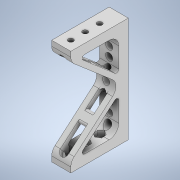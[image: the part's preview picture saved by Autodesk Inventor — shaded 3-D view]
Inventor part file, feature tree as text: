
AUTODESK INVENTOR PART (.ipt)
format: ipt  version: 2020 (Build 240168000, 168)  size: 472,576 bytes
history: native  units: in
note: dims shown in document units (in); Inventor stores cm internally (conversion verified against a paired STEP export)
features: extrude x10, sketch x10, plane x4, fillet x2, mirror x1
ambient origin geometry x8: Origin, YZ Plane, XZ Plane, XY Plane, X Axis, Y Axis, Z Axis, Center Point
bodies: Solid1 (feature_tree)
feature tree (27):
  extrude  "Extrusion1"  Depth=5.5in
  extrude  "Extrusion2"  Depth=0.5in
  fillet  "Fillet1"  Radius=0.5in
  extrude  "Extrusion3"  Depth=0.25in
  fillet  "Fillet2"  Radius=0.25in
  extrude  "Extrusion4"  Depth=0.5in
  plane  "Work Plane1"
  extrude  "Extrusion5"  Depth=0.125in
  extrude  "Extrusion6"  Depth=0.3937in
  plane  "Work Plane2"
  extrude  "Extrusion7"  [1 undecoded]
  plane  "Work Plane3"
  extrude  "Extrusion8"  Depth=0.3937in
  extrude  "Extrusion9"  Depth=0.25in
  extrude  "Extrusion10"  Depth=0.26in
  plane  "Work Plane4"
  mirror  "Mirror1"
  sketch  "Sketch1"  dims[d0=1.0in d1=5.5in]
  sketch  "Sketch2"  dims[d2=3.0in d3=0.0in d4=0.5in d5=0.5in]
  sketch  "Sketch3"  dims[d6=0.0in d7=0.0in d8=0.5in d9=0.25in]
  sketch  "Sketch4"  dims[d10=1.0in d11=0.0in d12=0.5in]
  sketch  "Sketch5"  dims[d13=0.125in d14=0.2in]
  sketch  "Sketch6"  dims[d16=2.5in d17=4.3307in d19=0.5in d20=0.3937in d22=1.0in]
  sketch  "Sketch7"  dims[d24=0.0in d25=0.0in d26=-0.25in]
  sketch  "Sketch8"  dims[d27=0.375in d28=3.5433in d30=0.5in d31=0.3937in d33=1.0in]
  sketch  "Sketch9"  dims[d35=0.25in d36=0.0in d37=1.0in]
  sketch  "Sketch10"  dims[d38=0.5in d39=0.2656in d40=1.1811in d42=0.75in d43=0.3937in d45=1.0in d47=0.0in d48=0.0in d49=-0.25in d50=0.4375in d51=2.5in d52=0.0in d53=-0.25in d54=0.4375in d55=2.5in d56=0.0in d57=0.26in d58=0.0in d59=0.375in d60=0.26in d61=0.0in]
note: 1 required parameter value undecoded (feature->parameter linkage not recoverable at this tier; creation-order binding heuristic only, values carry confidence <= 0.55)
